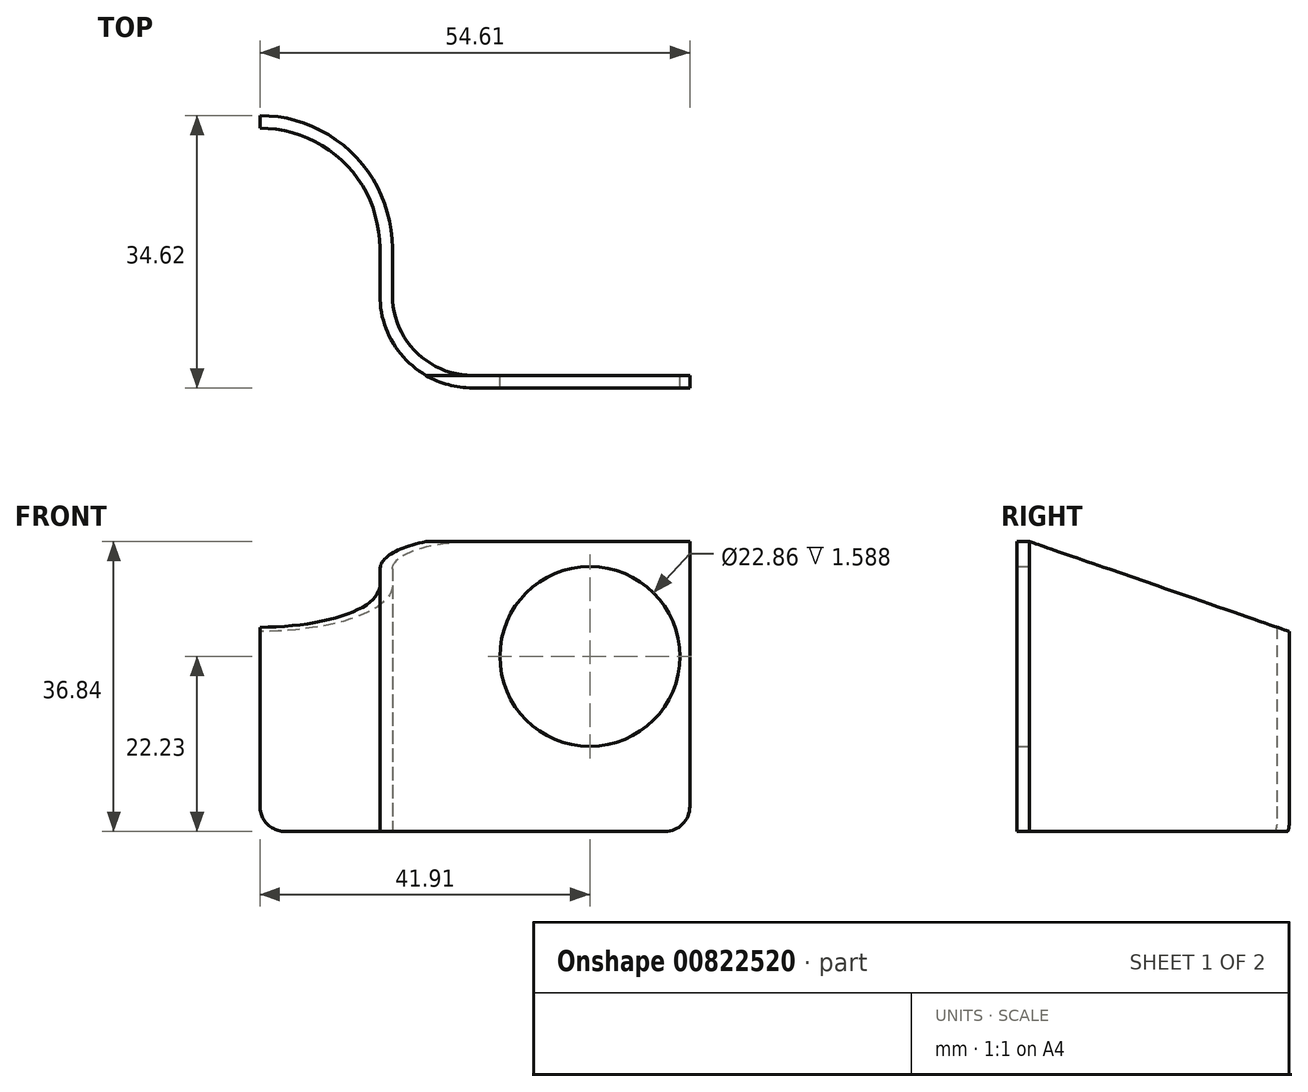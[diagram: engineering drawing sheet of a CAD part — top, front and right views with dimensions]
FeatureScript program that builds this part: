
annotation { "Feature Type Name" : "Feature", "Feature Type Description" : "" }
export const myFeature = defineFeature(function(context is Context, id is Id, definition is map)
    precondition{}
    {
        {
            var Q0;
            Q0=qCreatedBy(makeId("Front.planeOp"),FACE);
            var sketch = newSketch(context, id + "F0", { "sketchPlane" : qUnion([Q0])});
            skLineSegment(sketch, "E0.bottom", {"start": v(-41.9, -22.23) * mm, "end": v(12.7, -22.23) * mm});
            skLineSegment(sketch, "E0.top", {"start": v(-41.91, 53.98) * mm, "end": v(12.7, 53.98) * mm});
            skLineSegment(sketch, "E0.left", {"start": v(-41.9, -22.23) * mm, "end": v(-41.91, 53.98) * mm});
            skLineSegment(sketch, "E0.right", {"start": v(12.7, -22.23) * mm, "end": v(12.7, 53.98) * mm});
            skCircle(sketch, "E1", {"center": v(0, 0) * mm, "radius": 11.43 * mm});
            skSolve(sketch);
        }
        {
            var Q0;
            Q0=makeQuery(id+"F0.imprint","IMPRINT",FACE,{"disambiguationData":[TD([[makeQuery(id+"F0.imprint","IMPRINT",EDGE,{"derivedFrom":sQuery(id+"F0.wireOp",EDGE,"E0.bottom")}),1.0]])]});
            extrude(context, id + "F1", {"entities" : qUnion([Q0]), "endBound" : BoundingType.SYMMETRIC, "depth" : 152.4 * mm, "offsetDistance" : 25.4 * mm});
        }
        {
            var Q0;
            Q0=qCreatedBy(makeId("Top.planeOp"),FACE);
            var sketch = newSketch(context, id + "F2", { "sketchPlane" : qUnion([Q0])});
            skLineSegment(sketch, "E2", {"start": v(-14.92, 0) * mm, "end": v(12.7, 0) * mm});
            skLineSegment(sketch, "E3", {"start": v(-25.08, 10.16) * mm, "end": v(-25.08, 16.2) * mm});
            skLineSegment(sketch, "E4", {"start": v(-41.91, 33.03) * mm, "end": v(-67.3, 33.03) * mm});
            skPoint(sketch, "E5.visualSharp", {"position": v(-25.08, 33.03) * mm});
            skArc(sketch, "E5.filletArc", {"start": v(-25.08, 16.2) * mm, "mid": v(-30.01, 28.1) * mm, "end": v(-41.91, 33.03) * mm});
            skPoint(sketch, "E6.visualSharp", {"position": v(-25.08, 0) * mm});
            skArc(sketch, "E6.filletArc", {"start": v(-25.08, 10.16) * mm, "mid": v(-22.1, 2.98) * mm, "end": v(-14.92, 0) * mm});
            skLineSegment(sketch, "E7.0", {"start": v(-14.92, -1.59) * mm, "end": v(12.7, -1.59) * mm});
            skLineSegment(sketch, "E7.1", {"start": v(-41.91, 31.45) * mm, "end": v(-67.3, 31.45) * mm});
            skArc(sketch, "E7.2", {"start": v(-26.67, 16.2) * mm, "mid": v(-31.13, 26.98) * mm, "end": v(-41.91, 31.45) * mm});
            skLineSegment(sketch, "E7.3", {"start": v(-26.67, 10.16) * mm, "end": v(-26.67, 16.2) * mm});
            skArc(sketch, "E7.4", {"start": v(-26.67, 10.16) * mm, "mid": v(-23.23, 1.85) * mm, "end": v(-14.92, -1.59) * mm});
            skLineSegment(sketch, "E8", {"start": v(-67.31, 33.03) * mm, "end": v(-67.31, 31.45) * mm});
            skLineSegment(sketch, "E9", {"start": v(12.7, 0) * mm, "end": v(12.7, -1.59) * mm});
            skSolve(sketch);
        }
        {
            var Q0;
            Q0=makeQuery(id+"F2.imprint","IMPRINT",FACE,{"disambiguationData":[TD([[makeQuery(id+"F2.imprint","IMPRINT",EDGE,{"derivedFrom":sQuery(id+"F2.wireOp",EDGE,"E2")}),-1.0]])]});
            extrude(context, id + "F3", {"entities" : qUnion([Q0]), "operationType" : NewBodyOperationType.INTERSECT, "endBound" : BoundingType.SYMMETRIC, "depth" : 177.8 * mm, "offsetDistance" : 25.4 * mm});
        }
        {
            var Q0;
            Q0=qCreatedBy(makeId("Right.planeOp"),FACE);
            var sketch = newSketch(context, id + "F4", { "sketchPlane" : qUnion([Q0])});
            skLineSegment(sketch, "E10", {"start": v(0, 14.6) * mm, "end": v(33.03, 3.17) * mm});
            skLineSegment(sketch, "E11", {"start": v(33.03, 3.17) * mm, "end": v(33.03, -22.22) * mm});
            skLineSegment(sketch, "E12", {"start": v(33.03, -22.23) * mm, "end": v(-1.59, -22.23) * mm});
            skLineSegment(sketch, "E13", {"start": v(-1.59, -22.23) * mm, "end": v(-1.59, 14.6) * mm});
            skLineSegment(sketch, "E14", {"start": v(-1.59, 14.6) * mm, "end": v(0, 14.6) * mm});
            skSolve(sketch);
        }
        {
            var Q0;
            Q0=makeQuery(id+"F4.imprint","IMPRINT",FACE,{"disambiguationData":[TD([[makeQuery(id+"F4.imprint","IMPRINT",EDGE,{"derivedFrom":sQuery(id+"F4.wireOp",EDGE,"E10")}),-1.0]])]});
            extrude(context, id + "F5", {"entities" : qUnion([Q0]), "operationType" : NewBodyOperationType.INTERSECT, "endBound" : BoundingType.SYMMETRIC, "depth" : 203.2 * mm, "offsetDistance" : 25.4 * mm});
        }
        {
            var Q0;
            Q0=makeQuery(id+"F5.boolean.opBoolean","INTERSECT",EDGE,{"derivedFrom":[makeQuery(id+"F1.opExtrude","SWEPT_FACE",FACE,{"disambiguationData":[OSD([sQuery(id+"F0.wireOp",EDGE,"E0.right")])]}),makeQuery(id+"F5.boolean.toolComplement.opBoolean","COPY",FACE,{"derivedFrom":makeQuery(id+"F5.opExtrude","SWEPT_FACE",FACE,{"disambiguationData":[OSD([sQuery(id+"F4.wireOp",EDGE,"E14")])]})})]});
            var Q1;
            Q1=makeQuery(id+"F1.opExtrude","SWEPT_EDGE",EDGE,{"disambiguationData":[OSD([sQuery(id+"F0.wireOp",EDGE,"E0.bottom"),sQuery(id+"F0.wireOp",EDGE,"E0.right")])]});
            var Q2;
            Q2=makeQuery(id+"F5.boolean.opBoolean","INTERSECT",EDGE,{"derivedFrom":[makeQuery(id+"F1.opExtrude","SWEPT_FACE",FACE,{"disambiguationData":[OSD([sQuery(id+"F0.wireOp",EDGE,"E0.left")])]}),makeQuery(id+"F5.boolean.toolComplement.opBoolean","COPY",FACE,{"derivedFrom":makeQuery(id+"F5.opExtrude","SWEPT_FACE",FACE,{"disambiguationData":[OSD([sQuery(id+"F4.wireOp",EDGE,"E10")])]})})]});
            var Q3;
            Q3=makeQuery(id+"F1.opExtrude","SWEPT_EDGE",EDGE,{"disambiguationData":[OSD([sQuery(id+"F0.wireOp",EDGE,"E0.bottom"),sQuery(id+"F0.wireOp",EDGE,"E0.left")])]});
            fillet(context, id + "F6", {"entities" : qUnion([Q0, Q1, Q2, Q3]), "radius" : 3.17 * mm, "tangentPropagation" : true, "allowEdgeOverflow" : false});
        }
    });
